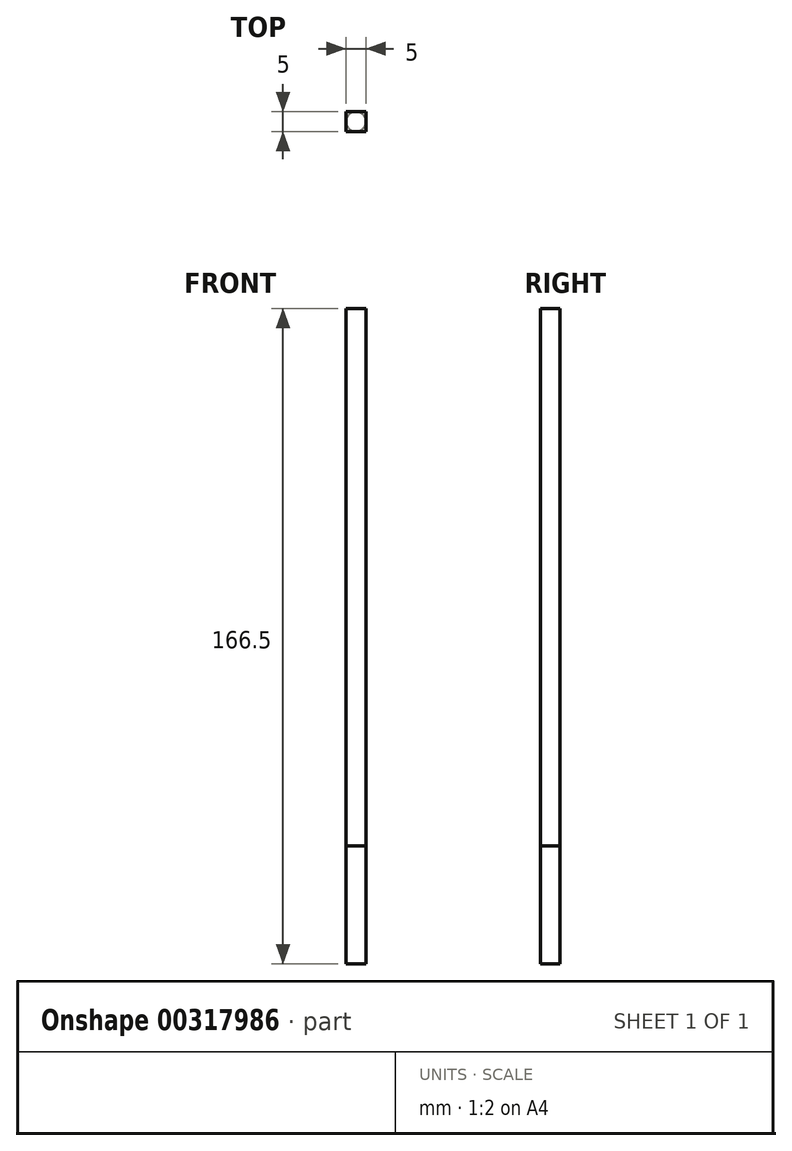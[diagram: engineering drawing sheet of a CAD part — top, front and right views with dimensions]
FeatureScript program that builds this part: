
annotation { "Feature Type Name" : "Feature", "Feature Type Description" : "" }
export const myFeature = defineFeature(function(context is Context, id is Id, definition is map)
    precondition{}
    {
        {
            var Q0;
            Q0=qCreatedBy(makeId("Top.planeOp"),FACE);
            var sketch = newSketch(context, id + "F0", { "sketchPlane" : qUnion([Q0])});
            skLineSegment(sketch, "E0.bottom", {"start": v(-2.61, 2.35) * mm, "end": v(2.39, 2.35) * mm});
            skLineSegment(sketch, "E0.top", {"start": v(-2.61, -2.65) * mm, "end": v(2.39, -2.65) * mm});
            skLineSegment(sketch, "E0.left", {"start": v(-2.61, 2.35) * mm, "end": v(-2.61, -2.65) * mm});
            skLineSegment(sketch, "E0.right", {"start": v(2.39, 2.35) * mm, "end": v(2.39, -2.65) * mm});
            skSolve(sketch);
        }
        {
            var Q0;
            Q0=qCreatedBy(makeId("Top.planeOp"),FACE);
            var sketch = newSketch(context, id + "F1", { "sketchPlane" : qUnion([Q0])});
            skCircle(sketch, "E1", {"center": v(-0.11, -0.15) * mm, "radius": 2.5 * mm});
            skSolve(sketch);
        }
        {
            var Q0;
            Q0=makeQuery(id+"F0.imprint","IMPRINT",FACE,{"disambiguationData":[TD([[makeQuery(id+"F0.imprint","IMPRINT",EDGE,{"derivedFrom":sQuery(id+"F0.wireOp",EDGE,"E0.bottom")}),-1.0]])]});
            extrude(context, id + "F2", {"entities" : qUnion([Q0]), "depth" : 136.5 * mm});
        }
        {
            var Q0;
            Q0=makeQuery(id+"F1.imprint","IMPRINT",FACE,{"disambiguationData":[TD([[makeQuery(id+"F1.imprint","IMPRINT",EDGE,{"derivedFrom":sQuery(id+"F1.wireOp",EDGE,"E1")}),1.0]])]});
            extrude(context, id + "F3", {"entities" : qUnion([Q0]), "operationType" : NewBodyOperationType.ADD, "oppositeDirection" : true, "depth" : 30 * mm});
        }
    });
